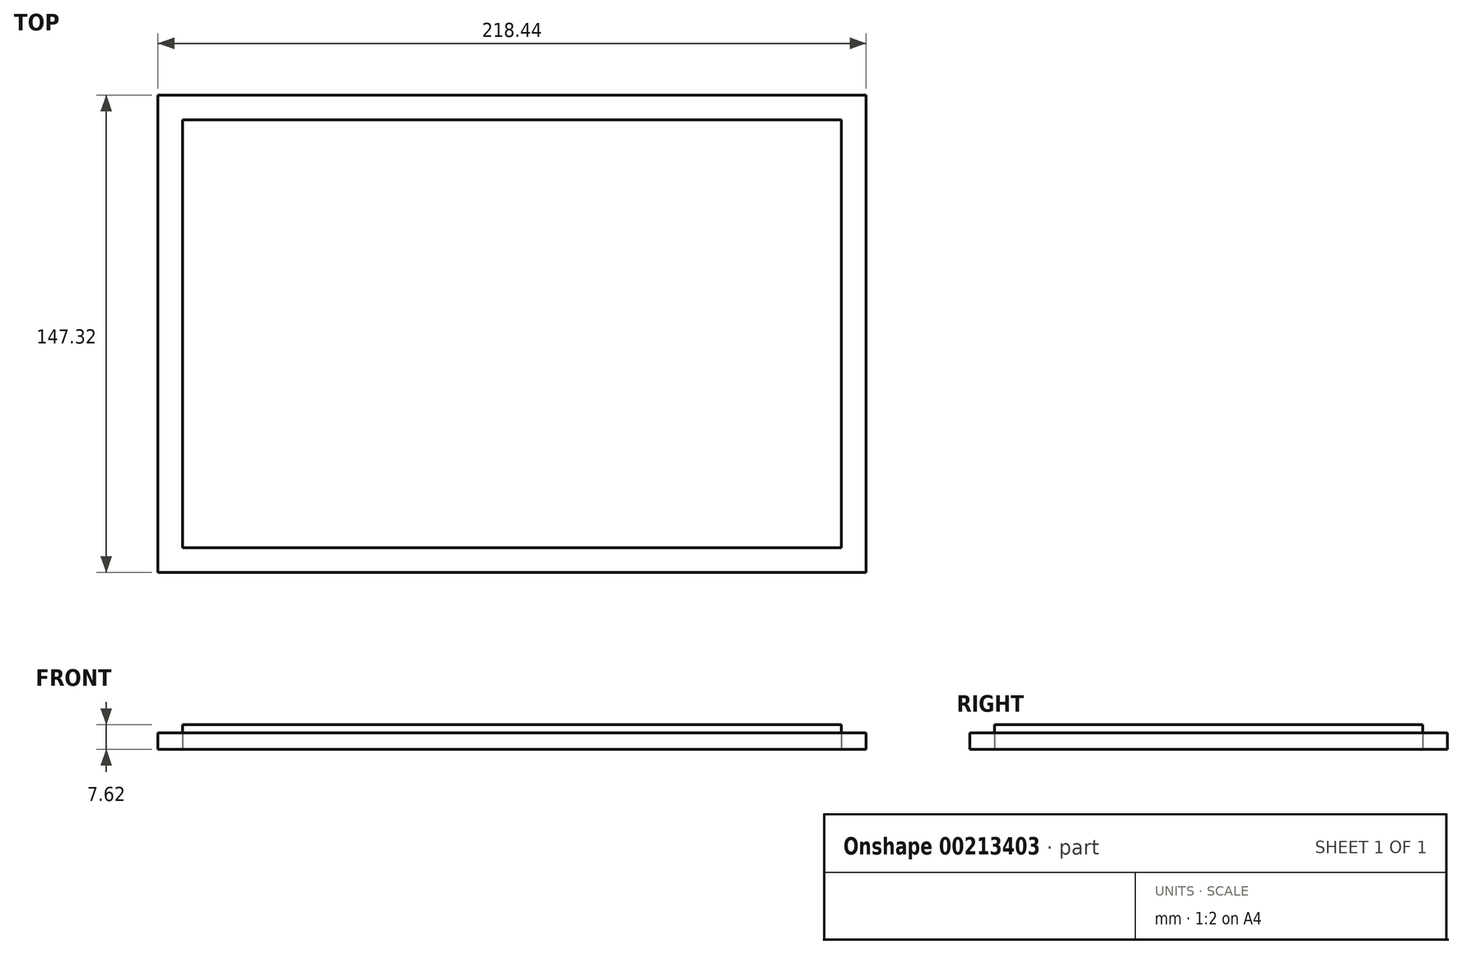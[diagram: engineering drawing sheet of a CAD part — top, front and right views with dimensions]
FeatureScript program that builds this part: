
annotation { "Feature Type Name" : "Feature", "Feature Type Description" : "" }
export const myFeature = defineFeature(function(context is Context, id is Id, definition is map)
    precondition{}
    {
        {
            var Q0;
            Q0=qCreatedBy(makeId("Top.planeOp"),FACE);
            var sketch = newSketch(context, id + "F0", { "sketchPlane" : qUnion([Q0])});
            skLineSegment(sketch, "E0.bottom", {"start": v(-109.22, 73.66) * mm, "end": v(109.22, 73.66) * mm});
            skLineSegment(sketch, "E0.top", {"start": v(-109.22, -73.66) * mm, "end": v(109.22, -73.66) * mm});
            skLineSegment(sketch, "E0.left", {"start": v(-109.22, 73.66) * mm, "end": v(-109.22, -73.66) * mm});
            skLineSegment(sketch, "E0.right", {"start": v(109.22, 73.66) * mm, "end": v(109.22, -73.66) * mm});
            skPoint(sketch, "E0.middle", {"position": v(0, 0) * mm});
            skSolve(sketch);
        }
        {
            var Q0;
            Q0 = qSketchRegion(id + "F0", true);
            extrude(context, id + "F1", {"entities" : qUnion([Q0]), "depth" : 5.08 * mm});
        }
        {
            var Q0;
            Q0=qCreatedBy(makeId("Top.planeOp"),FACE);
            var sketch = newSketch(context, id + "F2", { "sketchPlane" : qUnion([Q0])});
            skLineSegment(sketch, "E1.bottom", {"start": v(-101.6, 66.04) * mm, "end": v(101.6, 66.04) * mm});
            skLineSegment(sketch, "E1.top", {"start": v(-101.6, -66.04) * mm, "end": v(101.6, -66.04) * mm});
            skLineSegment(sketch, "E1.left", {"start": v(-101.6, 66.04) * mm, "end": v(-101.6, -66.04) * mm});
            skLineSegment(sketch, "E1.right", {"start": v(101.6, 66.04) * mm, "end": v(101.6, -66.04) * mm});
            skPoint(sketch, "E1.middle", {"position": v(0, 0) * mm});
            skSolve(sketch);
        }
        {
            var Q0;
            Q0 = qSketchRegion(id + "F2", true);
            extrude(context, id + "F3", {"entities" : qUnion([Q0]), "depth" : 7.62 * mm});
        }
    });
